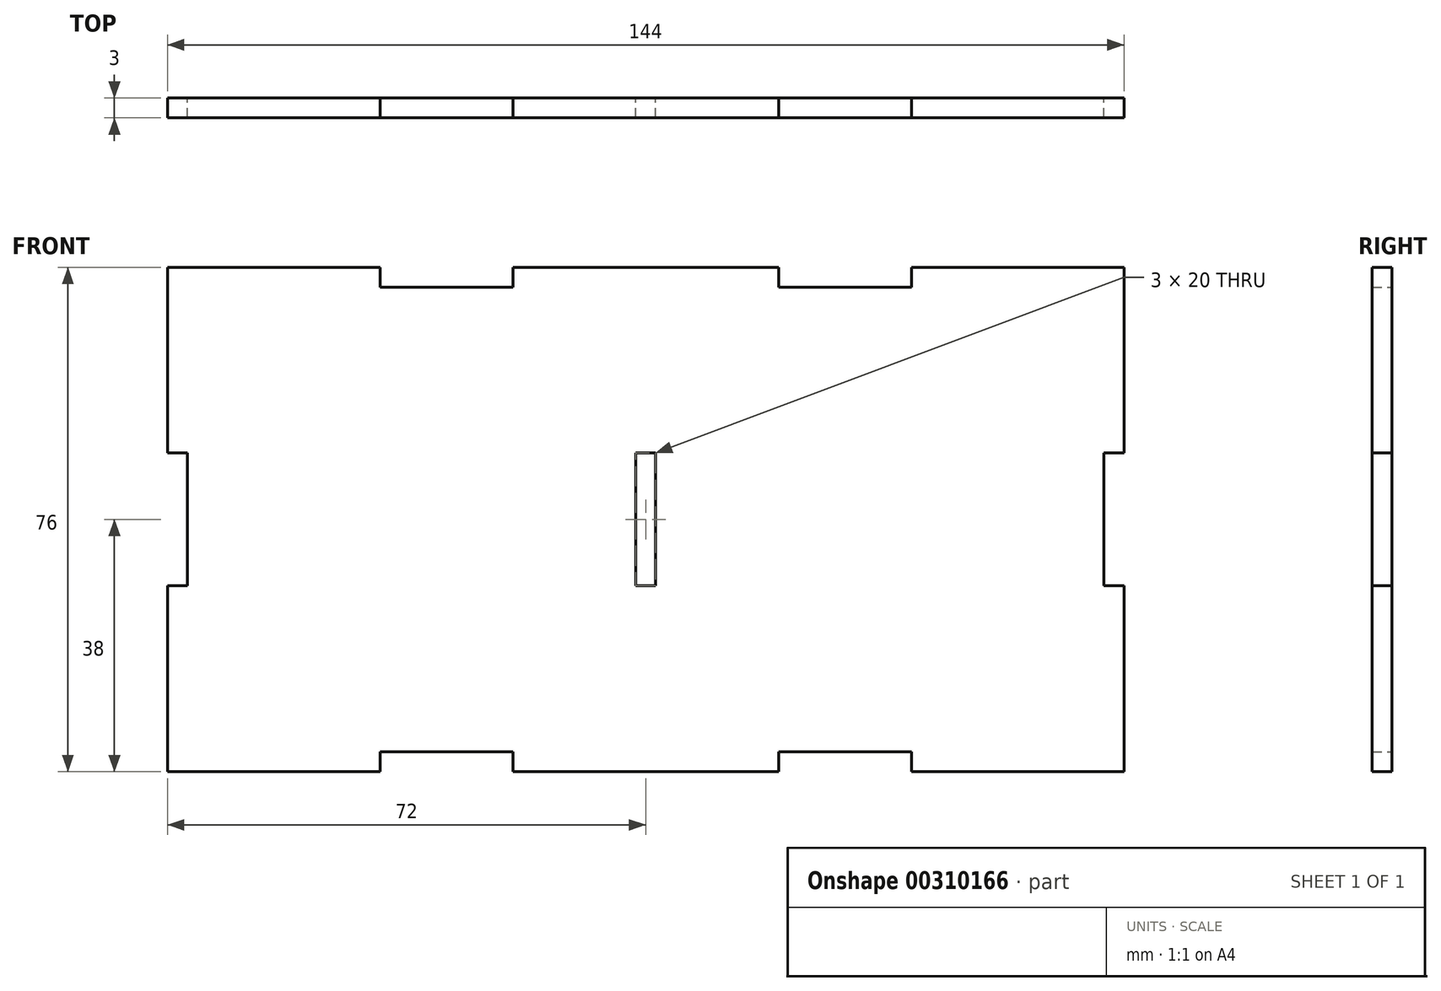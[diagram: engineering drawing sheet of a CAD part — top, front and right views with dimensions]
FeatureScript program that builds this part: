
annotation { "Feature Type Name" : "Feature", "Feature Type Description" : "" }
export const myFeature = defineFeature(function(context is Context, id is Id, definition is map)
    precondition{}
    {
        {
            var Q0;
            Q0=qCreatedBy(makeId("Front.planeOp"),FACE);
            var sketch = newSketch(context, id + "F0", { "sketchPlane" : qUnion([Q0])});
            skLineSegment(sketch, "E0.bottom", {"start": v(72, -38) * mm, "end": v(40, -38) * mm});
            skLineSegment(sketch, "E0.top", {"start": v(72, 38) * mm, "end": v(40, 38) * mm});
            skLineSegment(sketch, "E0.left", {"start": v(72, -38) * mm, "end": v(72, -10) * mm});
            skLineSegment(sketch, "E0.right", {"start": v(-72, -38) * mm, "end": v(-72, -10) * mm});
            skPoint(sketch, "E0.middle", {"position": v(0, 0) * mm});
            skLineSegment(sketch, "E1.bottom", {"start": v(-72, 10) * mm, "end": v(-69, 10) * mm});
            skLineSegment(sketch, "E1.top", {"start": v(-72, -10) * mm, "end": v(-69, -10) * mm});
            skLineSegment(sketch, "E1.right", {"start": v(-69, 10) * mm, "end": v(-69, -10) * mm});
            skLineSegment(sketch, "E2.top", {"start": v(-20, 35) * mm, "end": v(-40, 35) * mm});
            skLineSegment(sketch, "E2.left", {"start": v(-20, 38) * mm, "end": v(-20, 35) * mm});
            skLineSegment(sketch, "E2.right", {"start": v(-40, 38) * mm, "end": v(-40, 35) * mm});
            skLineSegment(sketch, "E3.MirrorCS", {"start": v(40, 38) * mm, "end": v(40, 35) * mm});
            skLineSegment(sketch, "E4.MirrorCS", {"start": v(20, 38) * mm, "end": v(20, 35) * mm});
            skLineSegment(sketch, "E5.MirrorCS", {"start": v(20, 35) * mm, "end": v(40, 35) * mm});
            skLineSegment(sketch, "E6.MirrorCS", {"start": v(69, 10) * mm, "end": v(69, -10) * mm});
            skLineSegment(sketch, "E7.MirrorCS", {"start": v(72, -10) * mm, "end": v(69, -10) * mm});
            skLineSegment(sketch, "E8.MirrorCS", {"start": v(72, 10) * mm, "end": v(69, 10) * mm});
            skLineSegment(sketch, "E9.MirrorCS", {"start": v(-40, -38) * mm, "end": v(-40, -35) * mm});
            skLineSegment(sketch, "E10.MirrorCS", {"start": v(-20, -38) * mm, "end": v(-20, -35) * mm});
            skLineSegment(sketch, "E11.MirrorCS", {"start": v(-20, -35) * mm, "end": v(-40, -35) * mm});
            skLineSegment(sketch, "E12.MirrorCS", {"start": v(40, -38) * mm, "end": v(40, -35) * mm});
            skLineSegment(sketch, "E13.MirrorCS", {"start": v(20, -38) * mm, "end": v(20, -35) * mm});
            skLineSegment(sketch, "E14.MirrorCS", {"start": v(20, -35) * mm, "end": v(40, -35) * mm});
            skLineSegment(sketch, "E15.trimOffspring", {"start": v(-40, 38) * mm, "end": v(-72, 38) * mm});
            skLineSegment(sketch, "E16.trimOffspring", {"start": v(-72, 10) * mm, "end": v(-72, 38) * mm});
            skLineSegment(sketch, "E17.trimOffspring", {"start": v(-40, -38) * mm, "end": v(-72, -38) * mm});
            skLineSegment(sketch, "E18.trimOffspring", {"start": v(20, -38) * mm, "end": v(-20, -38) * mm});
            skLineSegment(sketch, "E19.trimOffspring", {"start": v(20, 38) * mm, "end": v(-20, 38) * mm});
            skLineSegment(sketch, "E20.trimOffspring", {"start": v(72, 10) * mm, "end": v(72, 38) * mm});
            skLineSegment(sketch, "E21.bottom", {"start": v(1.5, -10) * mm, "end": v(-1.5, -10) * mm});
            skLineSegment(sketch, "E21.top", {"start": v(1.5, 10) * mm, "end": v(-1.5, 10) * mm});
            skLineSegment(sketch, "E21.left", {"start": v(1.5, -10) * mm, "end": v(1.5, 10) * mm});
            skLineSegment(sketch, "E21.right", {"start": v(-1.5, -10) * mm, "end": v(-1.5, 10) * mm});
            skSolve(sketch);
        }
        {
            var Q0;
            Q0 = qSketchRegion(id + "F0", true);
            extrude(context, id + "F1", {"entities" : qUnion([Q0]), "depth" : 3 * mm});
        }
    });
